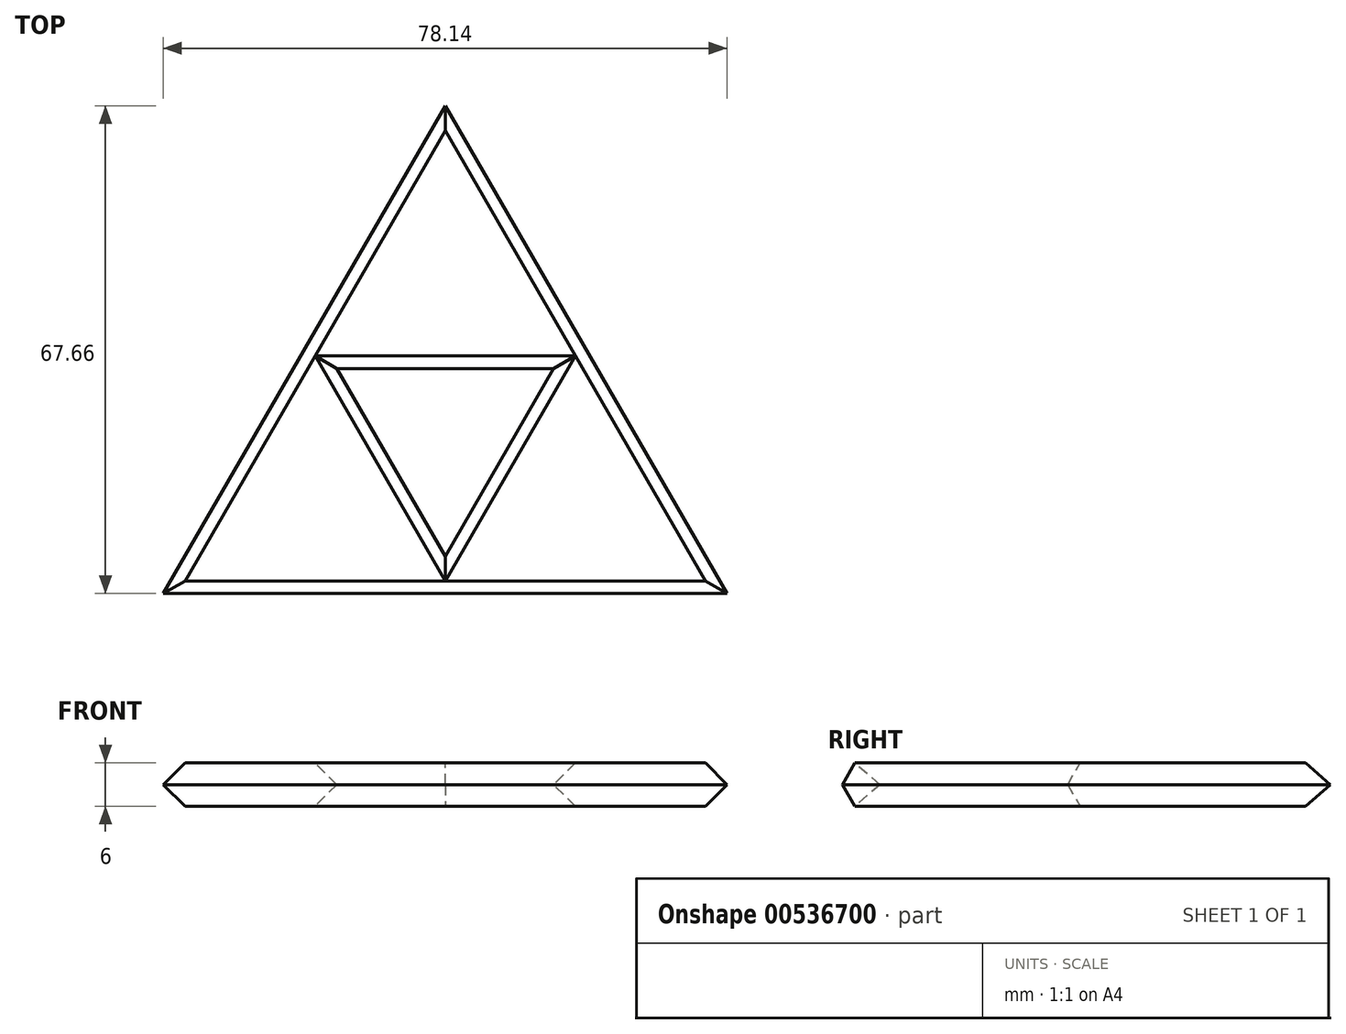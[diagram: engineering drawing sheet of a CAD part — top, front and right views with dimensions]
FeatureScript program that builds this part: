
annotation { "Feature Type Name" : "Feature", "Feature Type Description" : "" }
export const myFeature = defineFeature(function(context is Context, id is Id, definition is map)
    precondition{}
    {
        {
            var Q0;
            Q0=qCreatedBy(makeId("Top.planeOp"),FACE);
            var sketch = newSketch(context, id + "F0", { "sketchPlane" : qUnion([Q0])});
            skLineSegment(sketch, "E0", {"start": v(0, 42.53) * mm, "end": v(-36.07, -19.94) * mm});
            skLineSegment(sketch, "E1", {"start": v(-36.07, -19.94) * mm, "end": v(36.07, -19.94) * mm});
            skLineSegment(sketch, "E2", {"start": v(36.07, -19.94) * mm, "end": v(0, 42.53) * mm});
            skLineSegment(sketch, "E3", {"start": v(-18.03, 11.3) * mm, "end": v(18.03, 11.3) * mm});
            skLineSegment(sketch, "E4", {"start": v(18.03, 11.3) * mm, "end": v(0, -19.94) * mm});
            skLineSegment(sketch, "E5", {"start": v(0, -19.94) * mm, "end": v(-18.03, 11.3) * mm});
            skSolve(sketch);
        }
        {
            var Q0;
            {var subQ3=sQuery(id+"F0.wireOp",EDGE,"E4");Q0=makeQuery(id+"F0.imprint","IMPRINT",FACE,{"disambiguationData":[TD([[makeQuery(id+"F0.imprint","IMPRINT",EDGE,{"derivedFrom":subQ3}),1.0]])]});}
            var Q1;
            {var subQ3=sQuery(id+"F0.wireOp",EDGE,"E5");Q1=makeQuery(id+"F0.imprint","IMPRINT",FACE,{"disambiguationData":[TD([[makeQuery(id+"F0.imprint","IMPRINT",EDGE,{"derivedFrom":subQ3}),1.0]])]});}
            var Q2;
            {var subQ3=sQuery(id+"F0.wireOp",EDGE,"E3");Q2=makeQuery(id+"F0.imprint","IMPRINT",FACE,{"disambiguationData":[TD([[makeQuery(id+"F0.imprint","IMPRINT",EDGE,{"derivedFrom":subQ3}),1.0]])]});}
            extrude(context, id + "F1", {"entities" : qUnion([Q0, Q1, Q2]), "oppositeDirection" : true, "depth" : 3 * mm, "offsetDistance" : 25 * mm, "hasDraft" : true, "draftAngle" : 30 * degree});
        }
        {
            var Q0;
            Q0=makeQuery(id+"F1.opExtrude","SWEPT_BODY",BODY,{"disambiguationData":[OSD([sQuery(id+"F0.wireOp",EDGE,"E0"),sQuery(id+"F0.wireOp",EDGE,"E2"),sQuery(id+"F0.wireOp",EDGE,"E3")])]});
            var Q1;
            Q1=makeQuery(id+"F1.opExtrude","SWEPT_BODY",BODY,{"disambiguationData":[OSD([sQuery(id+"F0.wireOp",EDGE,"E0"),sQuery(id+"F0.wireOp",EDGE,"E1"),sQuery(id+"F0.wireOp",EDGE,"E5")])]});
            var Q2;
            Q2=makeQuery(id+"F1.opExtrude","SWEPT_BODY",BODY,{"disambiguationData":[OSD([sQuery(id+"F0.wireOp",EDGE,"E1"),sQuery(id+"F0.wireOp",EDGE,"E2"),sQuery(id+"F0.wireOp",EDGE,"E4")])]});
            booleanBodies(context, id + "F2", {"operationType" : BooleanOperationType.UNION, "tools" : qUnion([Q0, Q1, Q2])});
        }
        {
            var Q0;
            Q0=makeQuery(id+"F1.opExtrude","SWEPT_BODY",BODY,{"disambiguationData":[OSD([sQuery(id+"F0.wireOp",EDGE,"E0"),sQuery(id+"F0.wireOp",EDGE,"E2"),sQuery(id+"F0.wireOp",EDGE,"E3")])]});
            var Q1;
            {var subQ0=sQuery(id+"F0.wireOp",EDGE,"E2");var subQ1=sQuery(id+"F0.wireOp",EDGE,"E1");var subQ2=sQuery(id+"F0.wireOp",EDGE,"E0");Q1=makeQuery(id+"F2.opBoolean","MERGE",FACE,{"derivedFrom":[makeQuery(id+"F1.opExtrude","CAP_FACE",FACE,{"disambiguationData":[OSD([subQ2,subQ0,sQuery(id+"F0.wireOp",EDGE,"E3")])],"isStart":false}),makeQuery(id+"F1.opExtrude","CAP_FACE",FACE,{"disambiguationData":[OSD([subQ2,subQ1,sQuery(id+"F0.wireOp",EDGE,"E5")])],"isStart":false}),makeQuery(id+"F1.opExtrude","CAP_FACE",FACE,{"disambiguationData":[OSD([subQ1,subQ0,sQuery(id+"F0.wireOp",EDGE,"E4")])],"isStart":false})]});}
            mirror(context, id + "F3", {"operationType" : NewBodyOperationType.ADD, "entities" : qUnion([Q0]), "mirrorPlane" : qUnion([Q1])});
        }
    });
